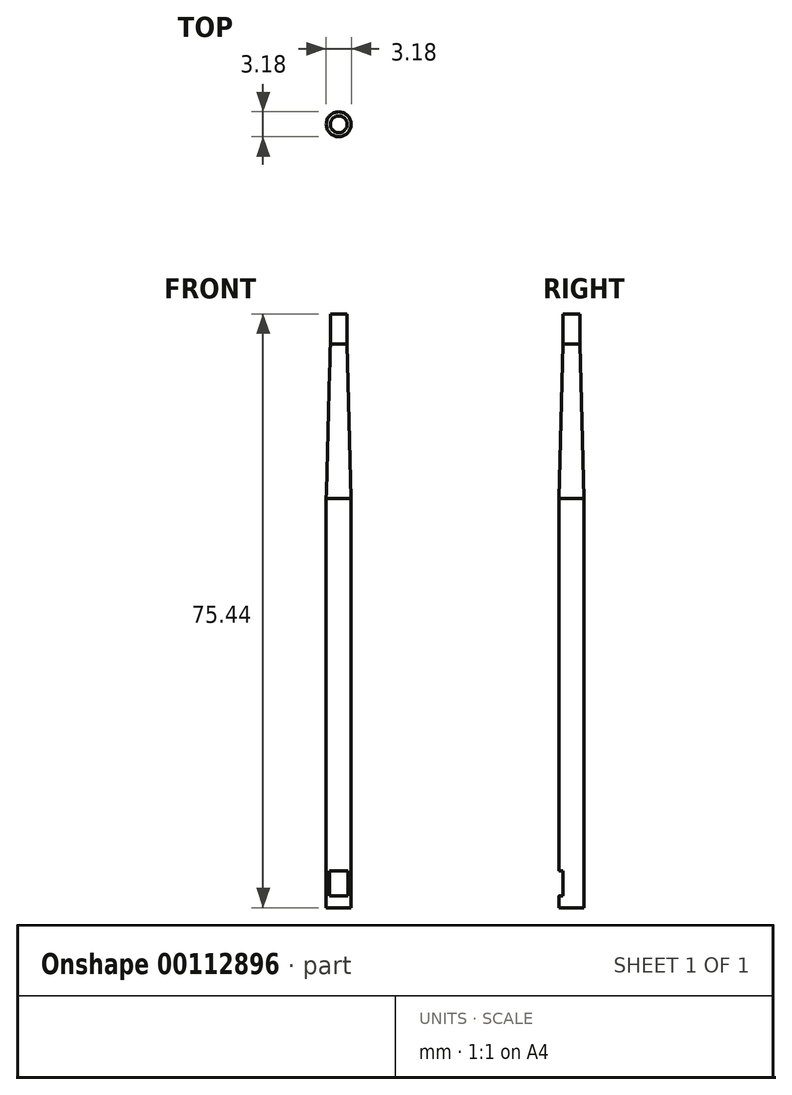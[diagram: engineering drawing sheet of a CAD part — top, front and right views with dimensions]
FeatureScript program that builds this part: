
annotation { "Feature Type Name" : "Feature", "Feature Type Description" : "" }
export const myFeature = defineFeature(function(context is Context, id is Id, definition is map)
    precondition{}
    {
        {
            var Q0;
            Q0=qCreatedBy(makeId("Front.planeOp"),FACE);
            var sketch = newSketch(context, id + "F0", { "sketchPlane" : qUnion([Q0])});
            skLineSegment(sketch, "E0", {"start": v(0, 0) * mm, "end": v(0, 75.44) * mm});
            skLineSegment(sketch, "E1", {"start": v(1.07, 75.44) * mm, "end": v(1.07, 71.63) * mm});
            skLineSegment(sketch, "E2", {"start": v(0, 75.44) * mm, "end": v(1.07, 75.44) * mm});
            skLineSegment(sketch, "E3", {"start": v(1.07, 71.63) * mm, "end": v(1.59, 51.99) * mm});
            skLineSegment(sketch, "E4", {"start": v(1.59, 0) * mm, "end": v(1.59, 51.99) * mm});
            skLineSegment(sketch, "E5", {"start": v(0, 0) * mm, "end": v(1.59, 0) * mm});
            skSolve(sketch);
        }
        {
            var Q0;
            Q0=makeQuery(id+"F0.imprint","IMPRINT",FACE,{"disambiguationData":[TD([[makeQuery(id+"F0.imprint","IMPRINT",EDGE,{"derivedFrom":sQuery(id+"F0.wireOp",EDGE,"E0")}),-1.0]])]});
            var Q1;
            Q1=sQuery(id+"F0.wireOp",EDGE,"E0");
            revolve(context, id + "F1", {"entities" : qUnion([Q0]), "axis" : qUnion([Q1]), "revolveType" : RevolveType.FULL});
        }
        {
            var Q0;
            Q0=qCreatedBy(makeId("Front.planeOp"),FACE);
            cPlane(context, id + "F2", {"entities" : qUnion([Q0]), "cplaneType" : CPlaneType.OFFSET, "offset" : 1.08 * mm, "width" : 152.4 * mm, "height" : 152.4 * mm});
        }
        {
            var Q0;
            Q0=qCreatedBy(id+"F2.planeOp",FACE);
            var sketch = newSketch(context, id + "F3", { "sketchPlane" : qUnion([Q0])});
            skLineSegment(sketch, "E6", {"start": v(-1.59, 1.52) * mm, "end": v(1.59, 1.52) * mm});
            skLineSegment(sketch, "E7", {"start": v(1.59, 1.52) * mm, "end": v(1.59, 4.7) * mm});
            skLineSegment(sketch, "E8", {"start": v(1.59, 4.7) * mm, "end": v(-1.59, 4.7) * mm});
            skLineSegment(sketch, "E9", {"start": v(-1.59, 4.7) * mm, "end": v(-1.59, 1.52) * mm});
            skSolve(sketch);
        }
        {
            var Q0;
            Q0=makeQuery(id+"F3.imprint","IMPRINT",FACE,{"disambiguationData":[TD([[makeQuery(id+"F3.imprint","IMPRINT",EDGE,{"derivedFrom":sQuery(id+"F3.wireOp",EDGE,"E6")}),1.0]])]});
            extrude(context, id + "F4", {"entities" : qUnion([Q0]), "operationType" : NewBodyOperationType.REMOVE, "depth" : 1.27 * mm});
        }
    });
